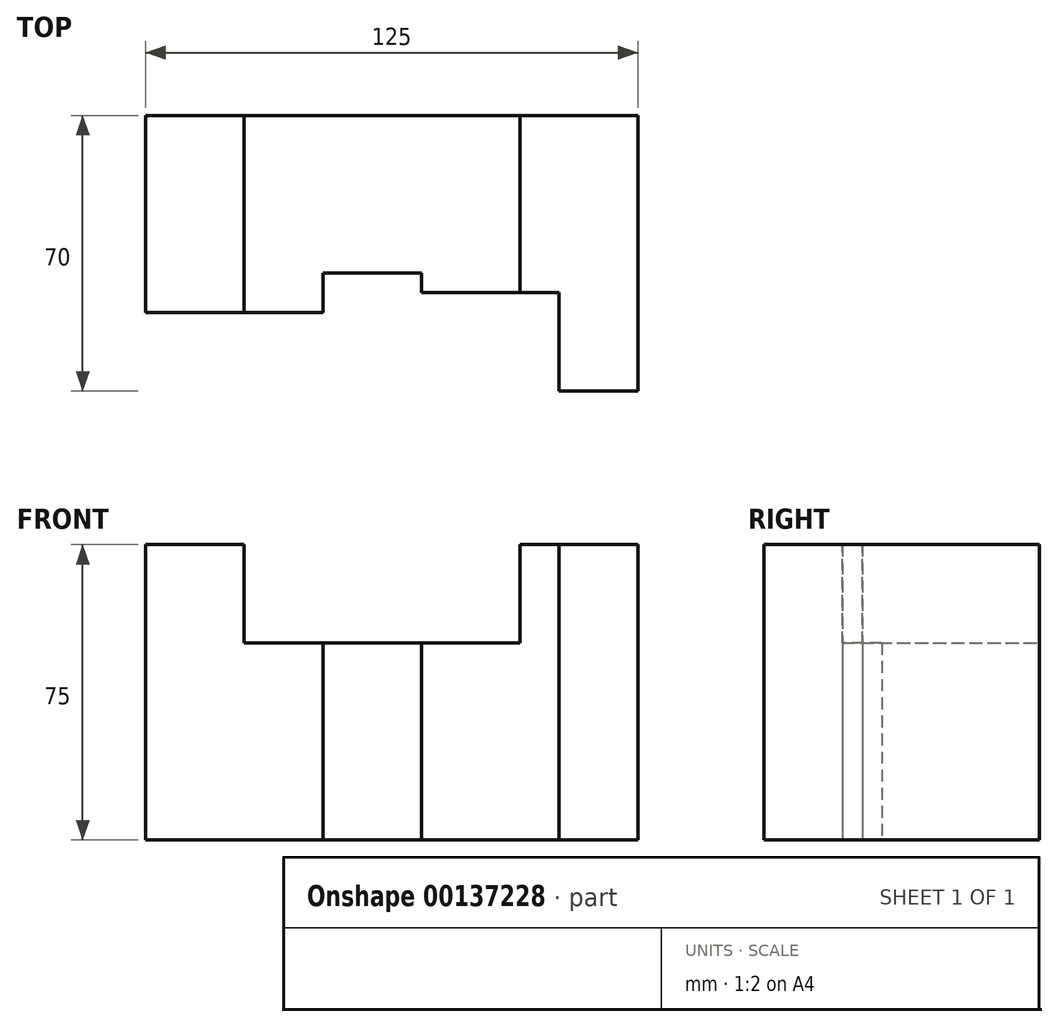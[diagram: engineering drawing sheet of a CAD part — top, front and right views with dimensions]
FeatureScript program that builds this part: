
annotation { "Feature Type Name" : "Feature", "Feature Type Description" : "" }
export const myFeature = defineFeature(function(context is Context, id is Id, definition is map)
    precondition{}
    {
        {
            var Q0;
            Q0=qCreatedBy(makeId("Top.planeOp"),FACE);
            var sketch = newSketch(context, id + "F0", { "sketchPlane" : qUnion([Q0])});
            skLineSegment(sketch, "E0", {"start": v(0, 0) * mm, "end": v(0, 50) * mm});
            skLineSegment(sketch, "E1", {"start": v(0, 50) * mm, "end": v(125, 50) * mm});
            skLineSegment(sketch, "E2", {"start": v(125, 50) * mm, "end": v(125, -20) * mm});
            skLineSegment(sketch, "E3", {"start": v(125, -20) * mm, "end": v(105, -20) * mm});
            skLineSegment(sketch, "E4", {"start": v(105, -20) * mm, "end": v(105, 5) * mm});
            skLineSegment(sketch, "E5", {"start": v(105, 5) * mm, "end": v(70, 5) * mm});
            skLineSegment(sketch, "E6", {"start": v(70, 5) * mm, "end": v(70, 10) * mm});
            skLineSegment(sketch, "E7", {"start": v(70, 10) * mm, "end": v(45, 10) * mm});
            skLineSegment(sketch, "E8", {"start": v(45, 10) * mm, "end": v(45, 0) * mm});
            skLineSegment(sketch, "E9", {"start": v(45, 0) * mm, "end": v(0, 0) * mm});
            skSolve(sketch);
        }
        {
            var Q0;
            Q0=makeQuery(id+"F0.imprint","IMPRINT",FACE,{"disambiguationData":[TD([[makeQuery(id+"F0.imprint","IMPRINT",EDGE,{"derivedFrom":sQuery(id+"F0.wireOp",EDGE,"E0")}),-1.0]])]});
            extrude(context, id + "F1", {"entities" : qUnion([Q0]), "depth" : (15 * 5) * mm});
        }
        {
            var Q0;
            Q0=makeQuery(id+"F1.opExtrude","CAP_FACE",FACE,{"disambiguationData":[OSD([sQuery(id+"F0.wireOp",EDGE,"E0"),sQuery(id+"F0.wireOp",EDGE,"E1"),sQuery(id+"F0.wireOp",EDGE,"E2"),sQuery(id+"F0.wireOp",EDGE,"E3"),sQuery(id+"F0.wireOp",EDGE,"E4"),sQuery(id+"F0.wireOp",EDGE,"E5"),sQuery(id+"F0.wireOp",EDGE,"E6"),sQuery(id+"F0.wireOp",EDGE,"E7"),sQuery(id+"F0.wireOp",EDGE,"E8"),sQuery(id+"F0.wireOp",EDGE,"E9")])],"isStart":false});
            var sketch = newSketch(context, id + "F2", { "sketchPlane" : qUnion([Q0])});
            skLineSegment(sketch, "E10", {"start": v(105, 5) * mm, "end": v(95, 5) * mm});
            skLineSegment(sketch, "E11", {"start": v(95, 5) * mm, "end": v(95, 50) * mm});
            skLineSegment(sketch, "E12", {"start": v(0, 0) * mm, "end": v(25, 0) * mm});
            skLineSegment(sketch, "E13", {"start": v(25, 0) * mm, "end": v(25, 50) * mm});
            skLineSegment(sketch, "E14", {"start": v(25, 50) * mm, "end": v(95, 50) * mm});
            skSolve(sketch);
        }
        {
            var Q0;
            {var subQ2=sQuery(id+"F2.wireOp",EDGE,"E11");Q0=makeQuery(id+"F2.imprint","IMPRINT",FACE,{"disambiguationData":[TD([[makeQuery(id+"F2.imprint","IMPRINT",EDGE,{"derivedFrom":subQ2}),1.0]])]});}
            extrude(context, id + "F3", {"entities" : qUnion([Q0]), "operationType" : NewBodyOperationType.REMOVE, "oppositeDirection" : true, "depth" : 25 * mm});
        }
    });
